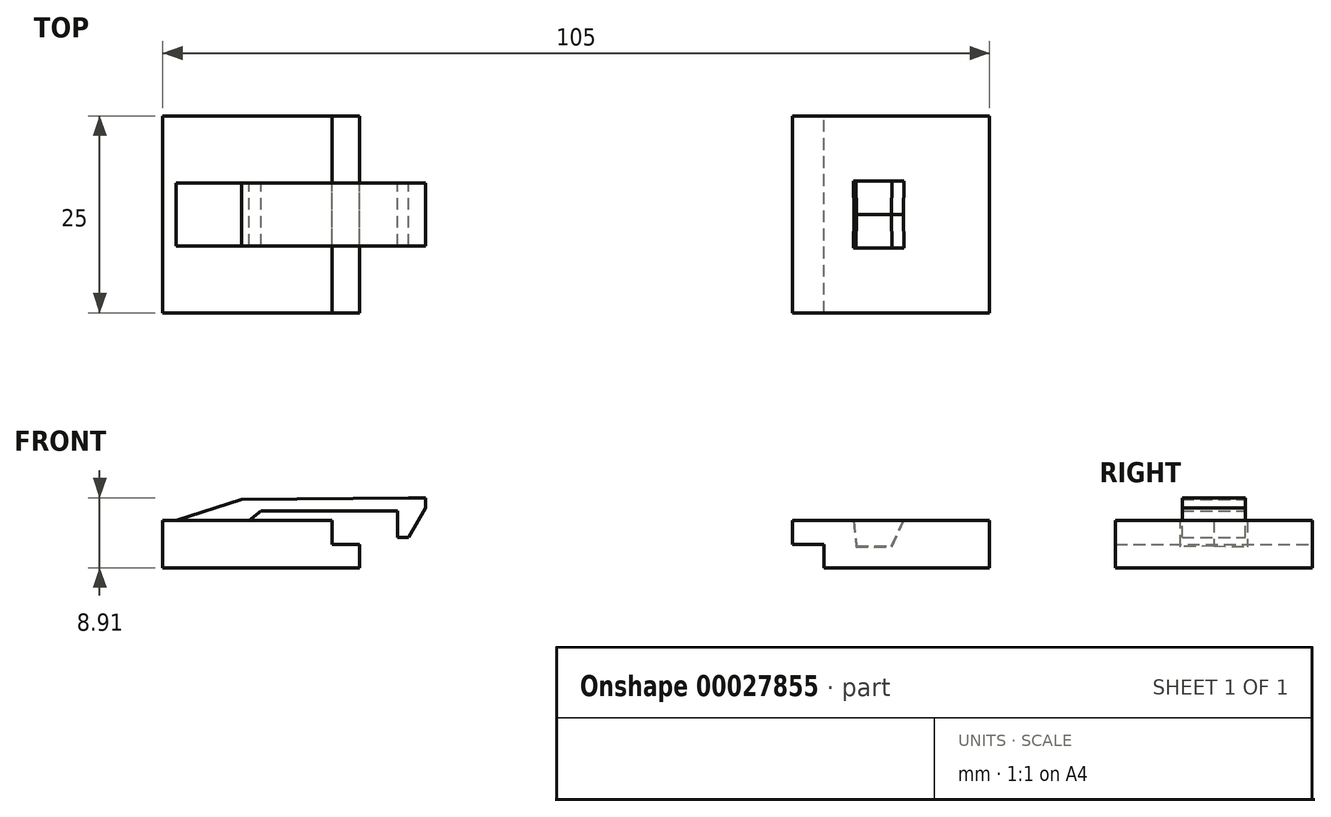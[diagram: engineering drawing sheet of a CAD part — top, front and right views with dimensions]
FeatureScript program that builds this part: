
annotation { "Feature Type Name" : "Feature", "Feature Type Description" : "" }
export const myFeature = defineFeature(function(context is Context, id is Id, definition is map)
    precondition{}
    {
        {
            var Q0;
            Q0=qCreatedBy(makeId("Top.planeOp"),FACE);
            var sketch = newSketch(context, id + "F0", { "sketchPlane" : qUnion([Q0])});
            skLineSegment(sketch, "E0.rect.bottom", {"start": v(52.5, -12.5) * mm, "end": v(27.5, -12.5) * mm});
            skLineSegment(sketch, "E0.rect.top", {"start": v(52.5, 12.5) * mm, "end": v(27.5, 12.5) * mm});
            skLineSegment(sketch, "E0.rect.left", {"start": v(52.5, -12.5) * mm, "end": v(52.5, 12.5) * mm});
            skLineSegment(sketch, "E0.rect.right", {"start": v(27.5, -12.5) * mm, "end": v(27.5, 12.5) * mm});
            skPoint(sketch, "E0.rect.middle", {"position": v(40, 0) * mm});
            skLineSegment(sketch, "E1.rect.bottom", {"start": v(-52.5, -12.5) * mm, "end": v(-27.5, -12.5) * mm});
            skLineSegment(sketch, "E1.rect.top", {"start": v(-52.5, 12.5) * mm, "end": v(-27.5, 12.5) * mm});
            skLineSegment(sketch, "E1.rect.left", {"start": v(-52.5, -12.5) * mm, "end": v(-52.5, 12.5) * mm});
            skLineSegment(sketch, "E1.rect.right", {"start": v(-27.5, -12.5) * mm, "end": v(-27.5, 12.5) * mm});
            skPoint(sketch, "E1.rect.middle", {"position": v(-40, 0) * mm});
            skSolve(sketch);
        }
        {
            var Q0;
            Q0=makeQuery(id+"F0.imprint","IMPRINT",FACE,{"disambiguationData":[TD([[makeQuery(id+"F0.imprint","IMPRINT",EDGE,{"derivedFrom":sQuery(id+"F0.wireOp",EDGE,"E0.rect.bottom")}),-1.0]])]});
            var Q1;
            Q1=makeQuery(id+"F0.imprint","IMPRINT",FACE,{"disambiguationData":[TD([[makeQuery(id+"F0.imprint","IMPRINT",EDGE,{"derivedFrom":sQuery(id+"F0.wireOp",EDGE,"E1.rect.bottom")}),1.0]])]});
            extrude(context, id + "F1", {"entities" : qUnion([Q0, Q1]), "depth" : 6 * mm});
        }
        {
            var Q0;
            Q0=makeQuery(id+"F1.opExtrude","SWEPT_FACE",FACE,{"disambiguationData":[OSD([sQuery(id+"F0.wireOp",EDGE,"E0.rect.right")])]});
            cPlane(context, id + "F2", {"entities" : qUnion([Q0]), "cplaneType" : CPlaneType.OFFSET, "offset" : 0 * mm, "width" : 150 * mm, "height" : 150 * mm});
        }
        {
            var Q0;
            Q0=qCreatedBy(id+"F2.planeOp",FACE);
            var sketch = newSketch(context, id + "F3", { "sketchPlane" : qUnion([Q0])});
            skLineSegment(sketch, "E2", {"start": v(12.5, 3) * mm, "end": v(-12.5, 3) * mm});
            skLineSegment(sketch, "E3.MirrorCS", {"start": v(12.5, 0) * mm, "end": v(12.5, 3) * mm});
            skLineSegment(sketch, "E4.MirrorCS", {"start": v(12.5, 0) * mm, "end": v(-12.5, 0) * mm});
            skLineSegment(sketch, "E5.MirrorCS", {"start": v(-12.5, 3) * mm, "end": v(-12.5, 0) * mm});
            skSolve(sketch);
        }
        {
            var Q0;
            Q0 = qSketchRegion(id + "F3", true);
            extrude(context, id + "F4", {"entities" : qUnion([Q0]), "operationType" : NewBodyOperationType.REMOVE, "oppositeDirection" : true, "depth" : 4 * mm});
        }
        {
            var Q0;
            Q0=makeQuery(id+"F1.opExtrude","SWEPT_FACE",FACE,{"disambiguationData":[OSD([sQuery(id+"F0.wireOp",EDGE,"E1.rect.right")])]});
            cPlane(context, id + "F5", {"entities" : qUnion([Q0]), "cplaneType" : CPlaneType.OFFSET, "offset" : 0 * mm, "width" : 150 * mm, "height" : 150 * mm});
        }
        {
            var Q0;
            Q0=qCreatedBy(id+"F5.planeOp",FACE);
            var sketch = newSketch(context, id + "F6", { "sketchPlane" : qUnion([Q0])});
            skLineSegment(sketch, "E6.0", {"start": v(-12.5, 6) * mm, "end": v(12.5, 6) * mm});
            skLineSegment(sketch, "E7", {"start": v(-12.5, 6) * mm, "end": v(-12.5, 3) * mm});
            skLineSegment(sketch, "E8", {"start": v(-12.5, 3) * mm, "end": v(12.5, 3) * mm});
            skLineSegment(sketch, "E9", {"start": v(12.5, 3) * mm, "end": v(12.5, 6) * mm});
            skSolve(sketch);
        }
        {
            var Q0;
            Q0 = qSketchRegion(id + "F6", true);
            extrude(context, id + "F7", {"entities" : qUnion([Q0]), "operationType" : NewBodyOperationType.REMOVE, "oppositeDirection" : true, "depth" : 3.5 * mm});
        }
        {
            var Q0;
            Q0=qCreatedBy(makeId("Front.planeOp"),FACE);
            var sketch = newSketch(context, id + "F8", { "sketchPlane" : qUnion([Q0])});
            skLineSegment(sketch, "E10", {"start": v(-22.7, 3.84) * mm, "end": v(-22.7, 7.26) * mm});
            skLineSegment(sketch, "E11", {"start": v(-21.28, 3.86) * mm, "end": v(-19.15, 7.63) * mm});
            skLineSegment(sketch, "E12", {"start": v(-21.26, 8.9) * mm, "end": v(-42.46, 8.7) * mm});
            skLineSegment(sketch, "E13", {"start": v(-22.7, 7.26) * mm, "end": v(-40, 7.26) * mm});
            skLineSegment(sketch, "E14.0", {"start": v(-50.8, 6) * mm, "end": v(-41.53, 6) * mm});
            skLineSegment(sketch, "E15", {"start": v(-42.46, 8.7) * mm, "end": v(-50.8, 6) * mm});
            skLineSegment(sketch, "E16", {"start": v(-40, 7.26) * mm, "end": v(-41.53, 6) * mm});
            skLineSegment(sketch, "E17", {"start": v(-19.15, 7.63) * mm, "end": v(-19.15, 8.9) * mm});
            skLineSegment(sketch, "E18", {"start": v(-19.15, 8.9) * mm, "end": v(-21.26, 8.9) * mm});
            skLineSegment(sketch, "E19", {"start": v(-22.7, 3.84) * mm, "end": v(-21.28, 3.86) * mm});
            skSolve(sketch);
        }
        {
            var Q0;
            Q0 = qSketchRegion(id + "F8", true);
            extrude(context, id + "F9", {"entities" : qUnion([Q0]), "operationType" : NewBodyOperationType.ADD, "endBound" : BoundingType.SYMMETRIC, "depth" : 8 * mm});
        }
        {
            var Q0;
            Q0=qCreatedBy(makeId("Front.planeOp"),FACE);
            var sketch = newSketch(context, id + "F10", { "sketchPlane" : qUnion([Q0])});
            skLineSegment(sketch, "E20", {"start": v(35.62, 2.77) * mm, "end": v(35.3, 6) * mm});
            skLineSegment(sketch, "E21.0", {"start": v(41.57, 6) * mm, "end": v(35.3, 6) * mm});
            skLineSegment(sketch, "E22", {"start": v(35.62, 2.77) * mm, "end": v(40.05, 2.77) * mm});
            skLineSegment(sketch, "E23", {"start": v(40.05, 2.77) * mm, "end": v(41.57, 6) * mm});
            skSolve(sketch);
        }
        {
            var Q0;
            Q0 = qSketchRegion(id + "F10", true);
            extrude(context, id + "F11", {"entities" : qUnion([Q0]), "operationType" : NewBodyOperationType.REMOVE, "endBound" : BoundingType.SYMMETRIC, "oppositeDirection" : true, "depth" : 8.5 * mm, "hasDraft" : true, "draftAngle" : 1 * degree});
        }
    });
